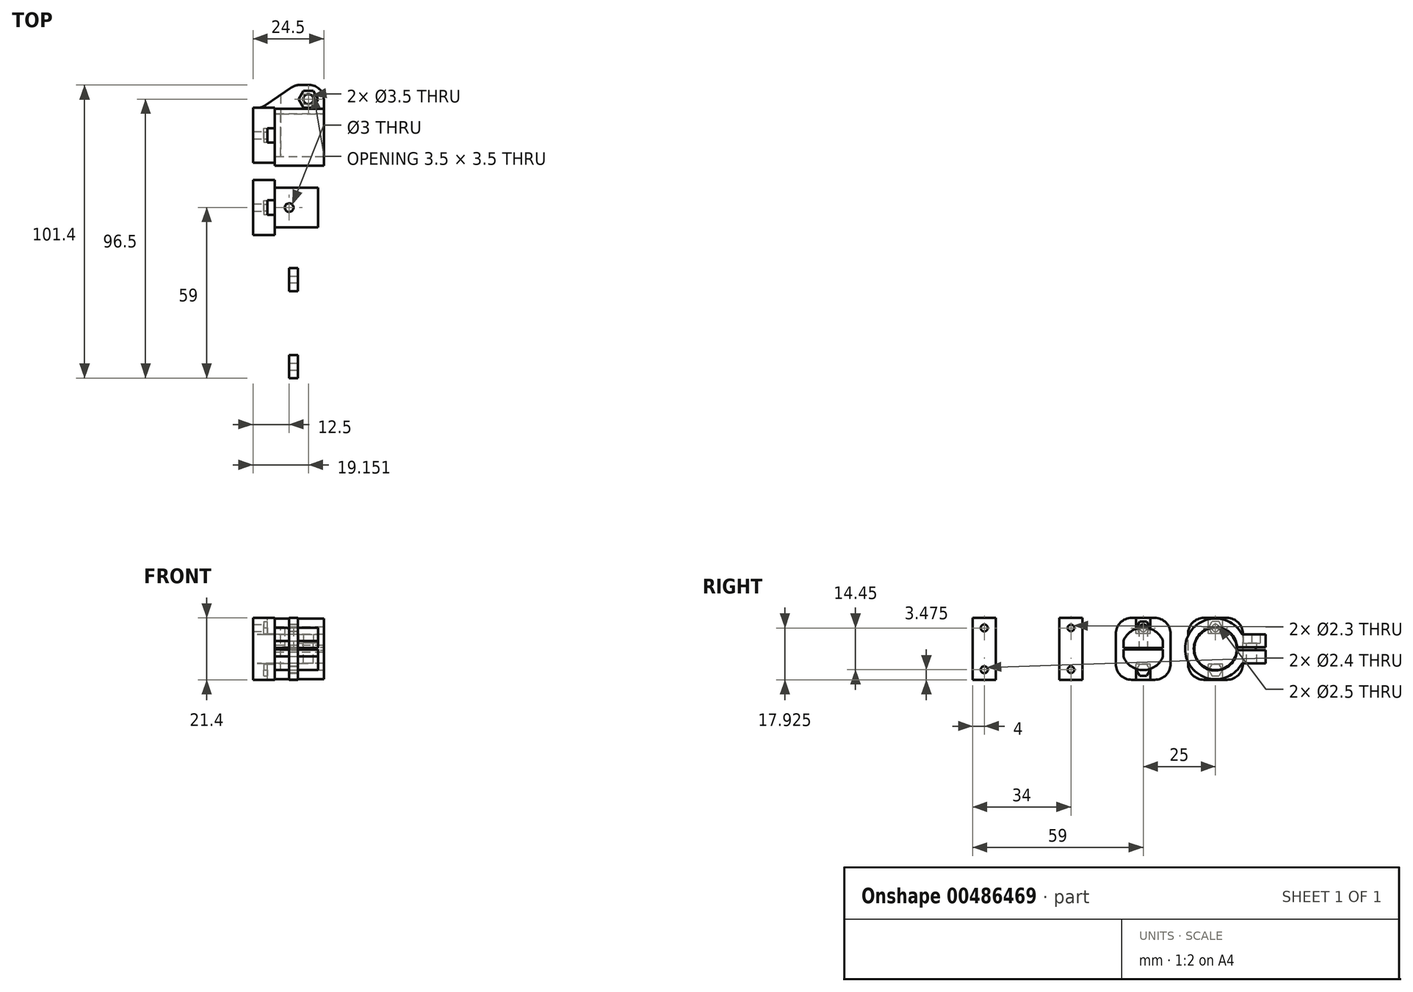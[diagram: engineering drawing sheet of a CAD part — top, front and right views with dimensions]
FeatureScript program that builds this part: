
annotation { "Feature Type Name" : "Feature", "Feature Type Description" : "" }
export const myFeature = defineFeature(function(context is Context, id is Id, definition is map)
    precondition{}
    {
        {
            assignVariable(context, id + "F0", {"name" : "nut_distance", "anyValue" : 5 * mm});
        }
        {
            var Q0;
            Q0=qCreatedBy(makeId("Front.planeOp"),FACE);
            var sketch = newSketch(context, id + "F1", { "sketchPlane" : qUnion([Q0])});
            skLineSegment(sketch, "E0", {"start": v(0, 3.75) * mm, "end": v(-7.5, 3.75) * mm});
            skLineSegment(sketch, "E1", {"start": v(-7.5, -3.75) * mm, "end": v(-7.5, 3.75) * mm});
            skLineSegment(sketch, "E2", {"start": v(-7.5, -3.75) * mm, "end": v(0, -3.75) * mm});
            skLineSegment(sketch, "E3", {"start": v(0, -10.7) * mm, "end": v(0, -3.75) * mm});
            skLineSegment(sketch, "E4", {"start": v(0, -10.7) * mm, "end": v(-12.5, -10.7) * mm});
            skLineSegment(sketch, "E5", {"start": v(-12.5, -10.7) * mm, "end": v(-12.5, 10.7) * mm});
            skLineSegment(sketch, "E6", {"start": v(0, 3.75) * mm, "end": v(0, 10.7) * mm});
            skLineSegment(sketch, "E7", {"start": v(-12.5, 10.7) * mm, "end": v(0, 10.7) * mm});
            skSolve(sketch);
        }
        {
            var Q0;
            Q0=qSketchRegion(id+"F1",true);
            extrude(context, id + "F2", {"entities" : qUnion([Q0]), "depth" : 8 * mm, "offsetDistance" : 25 * mm, "symmetric" : true});
        }
        {
            var Q0;
            Q0=makeQuery(id+"F2.opExtrude","SWEPT_FACE",FACE,{"disambiguationData":[OSD([sQuery(id+"F1.wireOp",EDGE,"E6")])]});
            var sketch = newSketch(context, id + "F3", { "sketchPlane" : qUnion([Q0])});
            skLineSegment(sketch, "E8", {"start": v(-12.42, 0) * mm, "end": v(17.97, 0) * mm, "construction": true});
            skLineSegment(sketch, "E9", {"start": v(0, 22.03) * mm, "end": v(0, -15.29) * mm, "construction": true});
            skPoint(sketch, "E9.startSnap0", {"position": v(0, 10.7) * mm});
            skLineSegment(sketch, "E10", {"start": v(0, 5.25) * mm, "end": v(-1.2, 5.25) * mm});
            skLineSegment(sketch, "E11", {"start": v(-1.2, 5.25) * mm, "end": v(-2.4, 7.32) * mm});
            skLineSegment(sketch, "E12", {"start": v(-2.4, 7.32) * mm, "end": v(0, 7.32) * mm, "construction": true});
            skLineSegment(sketch, "E13", {"start": v(0, 7.32) * mm, "end": v(1.2, 5.25) * mm, "construction": true});
            skLineSegment(sketch, "E14.MirrorCS", {"start": v(-1.2, 9.4) * mm, "end": v(-2.4, 7.32) * mm});
            skLineSegment(sketch, "E15.MirrorCS", {"start": v(0, 9.4) * mm, "end": v(-1.2, 9.4) * mm});
            skLineSegment(sketch, "E16.MirrorCS", {"start": v(0, 9.4) * mm, "end": v(1.2, 9.4) * mm});
            skLineSegment(sketch, "E17.MirrorCS", {"start": v(1.2, 9.4) * mm, "end": v(2.4, 7.33) * mm});
            skLineSegment(sketch, "E18.MirrorCS", {"start": v(1.2, 5.25) * mm, "end": v(2.4, 7.33) * mm});
            skLineSegment(sketch, "E19.MirrorCS", {"start": v(0, 5.25) * mm, "end": v(1.2, 5.25) * mm});
            skLineSegment(sketch, "E20.MirrorCS", {"start": v(-1.2, -9.4) * mm, "end": v(-2.4, -7.32) * mm});
            skLineSegment(sketch, "E21.MirrorCS", {"start": v(0, -9.4) * mm, "end": v(-1.2, -9.4) * mm});
            skLineSegment(sketch, "E22.MirrorCS", {"start": v(0, -9.4) * mm, "end": v(1.2, -9.4) * mm});
            skLineSegment(sketch, "E23.MirrorCS", {"start": v(1.2, -9.4) * mm, "end": v(2.4, -7.33) * mm});
            skLineSegment(sketch, "E24.MirrorCS", {"start": v(1.2, -5.25) * mm, "end": v(2.4, -7.33) * mm});
            skLineSegment(sketch, "E25.MirrorCS", {"start": v(0, -5.25) * mm, "end": v(1.2, -5.25) * mm});
            skLineSegment(sketch, "E26.MirrorCS", {"start": v(0, -5.25) * mm, "end": v(-1.2, -5.25) * mm});
            skLineSegment(sketch, "E27.MirrorCS", {"start": v(-1.2, -5.25) * mm, "end": v(-2.4, -7.32) * mm});
            skSolve(sketch);
        }
        {
            var Q0;
            Q0=makeQuery(id+"F3.imprint","IMPRINT",FACE,{"disambiguationData":[TD([[makeQuery(id+"F3.imprint","IMPRINT",EDGE,{"derivedFrom":sQuery(id+"F3.wireOp",EDGE,"E10")}),-1.0]])]});
            var Q1;
            Q1=makeQuery(id+"F3.imprint","IMPRINT",FACE,{"disambiguationData":[TD([[makeQuery(id+"F3.imprint","IMPRINT",EDGE,{"derivedFrom":sQuery(id+"F3.wireOp",EDGE,"E20.MirrorCS")}),-1.0]])]});
            extrude(context, id + "F4", {"entities" : qUnion([Q0, Q1]), "operationType" : NewBodyOperationType.REMOVE, "oppositeDirection" : true, "depth" : 5.4 * mm, "hasOffset" : true, "offsetDistance" : 4 * mm, "hasSecondDirection" : true, "secondDirectionOppositeDirection" : true, "secondDirectionDepth" : getVariable(context, 'nut_distance') - 1.3 * mm});
        }
        {
            var Q0;
            Q0=makeQuery(id+"F2.opExtrude","SWEPT_FACE",FACE,{"disambiguationData":[OSD([sQuery(id+"F1.wireOp",EDGE,"E7")])]});
            var sketch = newSketch(context, id + "F5", { "sketchPlane" : qUnion([Q0])});
            skLineSegment(sketch, "E28.bottom", {"start": v(-7.5, 2.5) * mm, "end": v(-5, 2.5) * mm});
            skLineSegment(sketch, "E28.top", {"start": v(-7.5, -2.5) * mm, "end": v(-5, -2.5) * mm});
            skLineSegment(sketch, "E28.left", {"start": v(-7.5, 2.5) * mm, "end": v(-7.5, -2.5) * mm});
            skLineSegment(sketch, "E28.right", {"start": v(-5, 2.5) * mm, "end": v(-5, -2.5) * mm});
            skSolve(sketch);
        }
        {
            var Q0;
            Q0=qSketchRegion(id+"F5",true);
            var Q1;
            Q1=makeQuery(id+"F4.boolean.opBoolean","COPY",VERTEX,{"derivedFrom":makeQuery(id+"F4.opExtrude","CAP_VERTEX",VERTEX,{"disambiguationData":[OSD([sQuery(id+"F3.wireOp",EDGE,"E10"),sQuery(id+"F3.wireOp",EDGE,"E11")])],"isStart":false})});
            extrude(context, id + "F6", {"entities" : qUnion([Q0]), "operationType" : NewBodyOperationType.REMOVE, "endBound" : BoundingType.UP_TO_VERTEX, "oppositeDirection" : true, "depth" : 25 * mm, "endBoundEntityVertex" : qUnion([Q1]), "offsetDistance" : 25 * mm});
        }
        {
            var Q0;
            Q0=makeQuery(id+"F2.opExtrude","SWEPT_FACE",FACE,{"disambiguationData":[OSD([sQuery(id+"F1.wireOp",EDGE,"E6")])]});
            var sketch = newSketch(context, id + "F7", { "sketchPlane" : qUnion([Q0])});
            skCircle(sketch, "E29", {"center": v(0, 7.22) * mm, "radius": 1.25 * mm});
            skCircle(sketch, "E30.MirrorC", {"center": v(0, -7.22) * mm, "radius": 1.25 * mm});
            skSolve(sketch);
        }
        {
            var Q0;
            Q0=makeQuery(id+"F7.imprint","IMPRINT",FACE,{"disambiguationData":[TD([[makeQuery(id+"F7.imprint","IMPRINT",EDGE,{"derivedFrom":sQuery(id+"F7.wireOp",EDGE,"E29")}),1.0]])]});
            var Q1;
            Q1=makeQuery(id+"F7.imprint","IMPRINT",FACE,{"disambiguationData":[TD([[makeQuery(id+"F7.imprint","IMPRINT",EDGE,{"derivedFrom":sQuery(id+"F7.wireOp",EDGE,"E30.MirrorC")}),-1.0]])]});
            var Q2;
            Q2=makeQuery(id+"F4.boolean.opBoolean","COPY",VERTEX,{"derivedFrom":makeQuery(id+"F4.opExtrude","CAP_VERTEX",VERTEX,{"disambiguationData":[OSD([sQuery(id+"F3.wireOp",EDGE,"E17.MirrorCS"),sQuery(id+"F3.wireOp",EDGE,"E18.MirrorCS")])],"isStart":false})});
            extrude(context, id + "F8", {"entities" : qUnion([Q0, Q1]), "operationType" : NewBodyOperationType.REMOVE, "endBound" : BoundingType.THROUGH_ALL, "oppositeDirection" : true, "depth" : 25 * mm, "endBoundEntityVertex" : qUnion([Q2]), "offsetDistance" : 25 * mm});
        }
        {
            var Q0;
            Q0=qSketchRegion(id+"F5",true);
            var Q1;
            Q1=makeQuery(id+"F2.opExtrude","SWEPT_FACE",FACE,{"disambiguationData":[OSD([sQuery(id+"F1.wireOp",EDGE,"E4")])]});
            var Q2;
            Q2=makeQuery(id+"F4.boolean.opBoolean","COPY",VERTEX,{"derivedFrom":makeQuery(id+"F4.opExtrude","CAP_VERTEX",VERTEX,{"disambiguationData":[OSD([sQuery(id+"F3.wireOp",EDGE,"E26.MirrorCS"),sQuery(id+"F3.wireOp",EDGE,"E27.MirrorCS")])],"isStart":false})});
            extrude(context, id + "F9", {"entities" : qUnion([Q0]), "operationType" : NewBodyOperationType.REMOVE, "endBound" : BoundingType.UP_TO_SURFACE, "oppositeDirection" : true, "depth" : 25 * mm, "endBoundEntityFace" : qUnion([Q1]), "offsetDistance" : 25 * mm, "hasSecondDirection" : true, "secondDirectionBound" : BoundingType.UP_TO_VERTEX, "secondDirectionOppositeDirection" : true, "secondDirectionDepth" : 25 * mm, "secondDirectionBoundEntityVertex" : qUnion([Q2])});
        }
        {
            var Q0;
            Q0=qSketchRegion(id+"F3",true);
            extrude(context, id + "F10", {"entities" : qUnion([Q0]), "operationType" : NewBodyOperationType.REMOVE, "oppositeDirection" : true, "depth" : (7.5 + 1.3) * mm, "offsetDistance" : 25 * mm, "hasSecondDirection" : true, "secondDirectionOppositeDirection" : true, "secondDirectionDepth" : (5.4 + 1.7) * mm});
        }
        {
            var Q0;
            Q0=qCreatedBy(makeId("Front.planeOp"),FACE);
            cPlane(context, id + "F11", {"entities" : qUnion([Q0]), "cplaneType" : CPlaneType.OFFSET, "offset" : 25 * mm, "width" : 150 * mm, "height" : 150 * mm});
        }
        {
            var Q0;
            Q0=qCreatedBy(makeId("Right.planeOp"),FACE);
            var sketch = newSketch(context, id + "F12", { "sketchPlane" : qUnion([Q0])});
            skLineSegment(sketch, "E31.bottom", {"start": v(-21, 10.7) * mm, "end": v(-29, 10.7) * mm});
            skLineSegment(sketch, "E31.top", {"start": v(-21, -10.7) * mm, "end": v(-29, -10.7) * mm});
            skLineSegment(sketch, "E31.left", {"start": v(-21, 10.7) * mm, "end": v(-21, -10.7) * mm});
            skLineSegment(sketch, "E31.right", {"start": v(-29, 10.7) * mm, "end": v(-29, -10.7) * mm});
            skCircle(sketch, "E32", {"center": v(-25, 7.22) * mm, "radius": 1.15 * mm});
            skCircle(sketch, "E33.MirrorC", {"center": v(-25, -7.22) * mm, "radius": 1.15 * mm});
            skSolve(sketch);
        }
        {
            var Q0;
            Q0=makeQuery(id+"F12.imprint","IMPRINT",FACE,{"disambiguationData":[TD([[makeQuery(id+"F12.imprint","IMPRINT",EDGE,{"derivedFrom":sQuery(id+"F12.wireOp",EDGE,"E31.bottom")}),1.0]])]});
            extrude(context, id + "F13", {"entities" : qUnion([Q0]), "depth" : 3 * mm, "offsetDistance" : 25 * mm});
        }
        {
            var Q0;
            Q0=qCreatedBy(id+"F11.planeOp",FACE);
            var sketch = newSketch(context, id + "F14", { "sketchPlane" : qUnion([Q0])});
            skArc(sketch, "E34", {"start": v(0, 3.75) * mm, "mid": v(-0.1, 0) * mm, "end": v(0, -3.75) * mm});
            skLineSegment(sketch, "E35", {"start": v(0, 3.75) * mm, "end": v(0, -3.75) * mm});
            skSolve(sketch);
        }
        {
            var Q0;
            Q0=makeQuery(id+"F13.opExtrude","SWEPT_BODY",BODY,{"disambiguationData":[OSD([sQuery(id+"F12.wireOp",EDGE,"E31.bottom"),sQuery(id+"F12.wireOp",EDGE,"E31.top"),sQuery(id+"F12.wireOp",EDGE,"E31.left"),sQuery(id+"F12.wireOp",EDGE,"E31.right"),sQuery(id+"F12.wireOp",EDGE,"E32"),sQuery(id+"F12.wireOp",EDGE,"E33.MirrorC")])]});
            transform(context, id + "F15", {"entities" : qUnion([Q0]), "transformType" : TransformType.TRANSLATION_3D, "dx" : 0 * mm, "dy" : -30 * mm, "dz" : 0 * mm, "makeCopy" : true});
        }
        {
            var Q0;
            Q0=makeQuery(id+"F15.opPattern","COPY",FACE,{"derivedFrom":makeQuery(id+"F13.opExtrude","CAP_FACE",FACE,{"disambiguationData":[OSD([sQuery(id+"F12.wireOp",EDGE,"E31.bottom"),sQuery(id+"F12.wireOp",EDGE,"E31.top"),sQuery(id+"F12.wireOp",EDGE,"E31.left"),sQuery(id+"F12.wireOp",EDGE,"E31.right"),sQuery(id+"F12.wireOp",EDGE,"E32"),sQuery(id+"F12.wireOp",EDGE,"E33.MirrorC")])],"isStart":false}),"instanceName":"1"});
            var sketch = newSketch(context, id + "F16", { "sketchPlane" : qUnion([Q0])});
            skCircle(sketch, "E36", {"center": v(-55, 7.22) * mm, "radius": 1.2 * mm});
            skCircle(sketch, "E37.MirrorC", {"center": v(-55, -7.22) * mm, "radius": 1.2 * mm});
            skSolve(sketch);
        }
        {
            var Q0;
            Q0=qSketchRegion(id+"F16",true);
            extrude(context, id + "F17", {"entities" : qUnion([Q0]), "operationType" : NewBodyOperationType.REMOVE, "endBound" : BoundingType.THROUGH_ALL, "oppositeDirection" : true, "depth" : 25 * mm, "offsetDistance" : 25 * mm});
        }
        {
            var Q0;
            Q0=qCreatedBy(makeId("Right.planeOp"),FACE);
            var sketch = newSketch(context, id + "F18", { "sketchPlane" : qUnion([Q0])});
            skCircle(sketch, "E38", {"center": v(0, 0) * mm, "radius": 7.35 * mm});
            skSolve(sketch);
        }
        {
            var Q0;
            Q0=makeQuery(id+"F2.opExtrude","SWEPT_FACE",FACE,{"disambiguationData":[OSD([sQuery(id+"F1.wireOp",EDGE,"E1")])]});
            var sketch = newSketch(context, id + "F19", { "sketchPlane" : qUnion([Q0])});
            skLineSegment(sketch, "E39.bottom", {"start": v(4, 3.75) * mm, "end": v(-4, 3.75) * mm});
            skLineSegment(sketch, "E39.top", {"start": v(4, -3.75) * mm, "end": v(-4, -3.75) * mm});
            skLineSegment(sketch, "E39.left", {"start": v(4, 3.75) * mm, "end": v(4, -3.75) * mm});
            skLineSegment(sketch, "E39.right", {"start": v(-4, 3.75) * mm, "end": v(-4, -3.75) * mm});
            skSolve(sketch);
        }
        {
            var Q0;
            Q0=qSketchRegion(id+"F19",true);
            var Q1;
            Q1=makeQuery(id+"F2.opExtrude","SWEPT_FACE",FACE,{"disambiguationData":[OSD([sQuery(id+"F1.wireOp",EDGE,"E6")])]});
            extrude(context, id + "F20", {"entities" : qUnion([Q0]), "operationType" : NewBodyOperationType.ADD, "endBound" : BoundingType.UP_TO_SURFACE, "depth" : 25 * mm, "endBoundEntityFace" : qUnion([Q1]), "offsetDistance" : 25 * mm});
        }
        {
            var Q0;
            Q0=qSketchRegion(id+"F18",true);
            extrude(context, id + "F21", {"entities" : qUnion([Q0]), "operationType" : NewBodyOperationType.ADD, "oppositeDirection" : true, "depth" : 5 * mm, "offsetDistance" : 25 * mm, "hasSecondDirection" : true, "secondDirectionOppositeDirection" : false, "secondDirectionDepth" : 10 * mm});
        }
        {
            var Q0;
            {var subQ0=sQuery(id+"F1.wireOp",EDGE,"E7");var subQ1=sQuery(id+"F1.wireOp",EDGE,"E6");var subQ4=sQuery(id+"F1.wireOp",EDGE,"E3");var subQ8=makeQuery(id+"F2.opExtrude","SWEPT_FACE",FACE,{"disambiguationData":[OSD([subQ1])]});var subQ9=sQuery(id+"F19.wireOp",EDGE,"E39.left");var subQ10=sQuery(id+"F19.wireOp",EDGE,"E39.right");Q0=makeQuery(id+"F21.boolean.opBoolean","SPLIT",FACE,{"disambiguationData":[TD([makeQuery(id+"F2.opExtrude","SWEPT_FACE",FACE,{"disambiguationData":[OSD([subQ0])]})])],"derivedFrom":makeQuery(id+"F20.boolean.opBoolean","MERGE",FACE,{"derivedFrom":[makeQuery(id+"F2.opExtrude","SWEPT_FACE",FACE,{"disambiguationData":[OSD([subQ4])]}),subQ8,makeQuery(id+"F20.opExtrude","CAP_FACE",FACE,{"disambiguationData":[OSD([sQuery(id+"F19.wireOp",EDGE,"E39.bottom"),sQuery(id+"F19.wireOp",EDGE,"E39.top"),subQ9,subQ10])],"isStart":false})]})});}
            var sketch = newSketch(context, id + "F22", { "sketchPlane" : qUnion([Q0])});
            skArc(sketch, "E40", {"start": v(4, 6.17) * mm, "mid": v(0, 7.35) * mm, "end": v(-4, 6.17) * mm});
            skLineSegment(sketch, "E41", {"start": v(-4, 6.17) * mm, "end": v(-4, 10.7) * mm});
            skLineSegment(sketch, "E42", {"start": v(-4, 10.7) * mm, "end": v(4, 10.7) * mm});
            skLineSegment(sketch, "E43", {"start": v(4, 10.7) * mm, "end": v(4, 6.17) * mm});
            skArc(sketch, "E44.MirrorCS", {"start": v(4, -6.17) * mm, "mid": v(0, -7.35) * mm, "end": v(-4, -6.17) * mm});
            skLineSegment(sketch, "E45.MirrorCS", {"start": v(-4, -10.7) * mm, "end": v(4, -10.7) * mm});
            skLineSegment(sketch, "E46.MirrorCS", {"start": v(-4, -6.17) * mm, "end": v(-4, -10.7) * mm});
            skLineSegment(sketch, "E47.MirrorCS", {"start": v(4, -10.7) * mm, "end": v(4, -6.17) * mm});
            skSolve(sketch);
        }
        {
            var Q0;
            Q0=qSketchRegion(id+"F22",true);
            extrude(context, id + "F23", {"entities" : qUnion([Q0]), "operationType" : NewBodyOperationType.REMOVE, "oppositeDirection" : true, "depth" : 5 * mm, "offsetDistance" : 25 * mm});
        }
        {
            var Q0;
            Q0=makeQuery(id+"F2.opExtrude","SWEPT_FACE",FACE,{"disambiguationData":[OSD([sQuery(id+"F1.wireOp",EDGE,"E5")])]});
            var sketch = newSketch(context, id + "F24", { "sketchPlane" : qUnion([Q0])});
            skPoint(sketch, "E48", {"position": v(4, -10.7) * mm});
            skPoint(sketch, "E49", {"position": v(4, 10.7) * mm});
            skLineSegment(sketch, "E50.bottom", {"start": v(9.5, -10.7) * mm, "end": v(4, -10.7) * mm});
            skLineSegment(sketch, "E50.top", {"start": v(9.5, 10.7) * mm, "end": v(4, 10.7) * mm});
            skLineSegment(sketch, "E50.left", {"start": v(9.5, -10.7) * mm, "end": v(9.5, 10.7) * mm});
            skLineSegment(sketch, "E50.right", {"start": v(4, -10.7) * mm, "end": v(4, 10.7) * mm});
            skPoint(sketch, "E51.MirrorP", {"position": v(-4, 10.7) * mm});
            skPoint(sketch, "E52.MirrorP", {"position": v(-4, -10.7) * mm});
            skLineSegment(sketch, "E53.MirrorCS", {"start": v(-9.5, -10.7) * mm, "end": v(-4, -10.7) * mm});
            skLineSegment(sketch, "E54.MirrorCS", {"start": v(-4, -10.7) * mm, "end": v(-4, 10.7) * mm});
            skLineSegment(sketch, "E55.MirrorCS", {"start": v(-9.5, -10.7) * mm, "end": v(-9.5, 10.7) * mm});
            skLineSegment(sketch, "E56.MirrorCS", {"start": v(-9.5, 10.7) * mm, "end": v(-4, 10.7) * mm});
            skSolve(sketch);
        }
        {
            var Q0;
            Q0=qSketchRegion(id+"F24",true);
            var Q1;
            {var subQ0=sQuery(id+"F18.wireOp",EDGE,"E38");Q1=makeQuery(id+"F21.boolean.opBoolean","SPLIT",FACE,{"disambiguationData":[TD([makeQuery(id+"F20.opExtrude","SWEPT_FACE",FACE,{"disambiguationData":[OSD([sQuery(id+"F19.wireOp",EDGE,"E39.right")])]})])],"derivedFrom":makeQuery(id+"F21.opExtrude","CAP_FACE",FACE,{"disambiguationData":[OSD([subQ0])],"isStart":false})});}
            extrude(context, id + "F25", {"entities" : qUnion([Q0]), "operationType" : NewBodyOperationType.ADD, "endBound" : BoundingType.UP_TO_SURFACE, "oppositeDirection" : true, "depth" : 5 * mm, "endBoundEntityFace" : qUnion([Q1]), "offsetDistance" : 25 * mm});
        }
        {
            var Q0;
            Q0=makeQuery(id+"F25.opExtrude","SWEPT_EDGE",EDGE,{"disambiguationData":[OSD([sQuery(id+"F24.wireOp",EDGE,"E50.top"),sQuery(id+"F24.wireOp",EDGE,"E50.left")])]});
            var Q1;
            Q1=makeQuery(id+"F25.opExtrude","SWEPT_EDGE",EDGE,{"disambiguationData":[OSD([sQuery(id+"F24.wireOp",EDGE,"E55.MirrorCS"),sQuery(id+"F24.wireOp",EDGE,"E56.MirrorCS")])]});
            var Q2;
            Q2=makeQuery(id+"F25.opExtrude","SWEPT_EDGE",EDGE,{"disambiguationData":[OSD([sQuery(id+"F24.wireOp",EDGE,"E53.MirrorCS"),sQuery(id+"F24.wireOp",EDGE,"E55.MirrorCS")])]});
            var Q3;
            Q3=makeQuery(id+"F25.opExtrude","SWEPT_EDGE",EDGE,{"disambiguationData":[OSD([sQuery(id+"F24.wireOp",EDGE,"E50.bottom"),sQuery(id+"F24.wireOp",EDGE,"E50.left")])]});
            fillet(context, id + "F26", {"entities" : qUnion([Q0, Q1, Q2, Q3]), "radius" : 5.5 * mm, "tangentPropagation" : true, "allowEdgeOverflow" : false});
        }
        {
            var Q0;
            Q0=qCreatedBy(makeId("Top.planeOp"),FACE);
            var sketch = newSketch(context, id + "F27", { "sketchPlane" : qUnion([Q0])});
            skCircle(sketch, "E57", {"center": v(0, 0) * mm, "radius": 1.5 * mm});
            skSolve(sketch);
        }
        {
            var Q0;
            Q0=qSketchRegion(id+"F27",true);
            extrude(context, id + "F28", {"entities" : qUnion([Q0]), "operationType" : NewBodyOperationType.REMOVE, "depth" : 25 * mm, "offsetDistance" : 25 * mm, "hasSecondDirection" : true, "secondDirectionOppositeDirection" : false, "secondDirectionDepth" : 0 * mm});
        }
        {
            var Q0;
            Q0=qCreatedBy(makeId("Front.planeOp"),FACE);
            cPlane(context, id + "F29", {"entities" : qUnion([Q0]), "cplaneType" : CPlaneType.OFFSET, "offset" : 25 * mm, "oppositeDirection" : true, "width" : 150 * mm, "height" : 150 * mm});
        }
        {
            var Q0;
            Q0=makeQuery(id+"F2.opExtrude","SWEPT_BODY",BODY,{"disambiguationData":[OSD([sQuery(id+"F1.wireOp",EDGE,"E0"),sQuery(id+"F1.wireOp",EDGE,"E1"),sQuery(id+"F1.wireOp",EDGE,"E2"),sQuery(id+"F1.wireOp",EDGE,"E3"),sQuery(id+"F1.wireOp",EDGE,"E4"),sQuery(id+"F1.wireOp",EDGE,"E5"),sQuery(id+"F1.wireOp",EDGE,"E6"),sQuery(id+"F1.wireOp",EDGE,"E7")])]});
            transform(context, id + "F30", {"entities" : qUnion([Q0]), "transformType" : TransformType.TRANSLATION_3D, "dx" : 0 * mm, "dy" : 25 * mm, "dz" : 0 * mm, "makeCopy" : true});
        }
        {
            var Q0;
            Q0=qCreatedBy(makeId("Right.planeOp"),FACE);
            var sketch = newSketch(context, id + "F31", { "sketchPlane" : qUnion([Q0])});
            skCircle(sketch, "E58", {"center": v(25, 0) * mm, "radius": 7.35 * mm});
            skSolve(sketch);
        }
        {
            var Q0;
            Q0=qCreatedBy(makeId("Right.planeOp"),FACE);
            var sketch = newSketch(context, id + "F32", { "sketchPlane" : qUnion([Q0])});
            skCircle(sketch, "E59", {"center": v(25, 0) * mm, "radius": 7.5 * mm});
            skCircle(sketch, "E60", {"center": v(25, 0) * mm, "radius": 10.5 * mm});
            skSolve(sketch);
        }
        {
            var Q0;
            Q0=qSketchRegion(id+"F32",true);
            extrude(context, id + "F33", {"entities" : qUnion([Q0]), "operationType" : NewBodyOperationType.ADD, "depth" : 12 * mm, "offsetDistance" : 25 * mm, "hasSecondDirection" : true, "secondDirectionOppositeDirection" : true, "secondDirectionDepth" : 5 * mm});
        }
        {
            var Q0;
            Q0=qSketchRegion(id+"F31",true);
            extrude(context, id + "F34", {"entities" : qUnion([Q0]), "operationType" : NewBodyOperationType.REMOVE, "oppositeDirection" : true, "depth" : 3 * mm, "offsetDistance" : 25 * mm, "hasSecondDirection" : true, "secondDirectionOppositeDirection" : false, "secondDirectionDepth" : 10 * mm});
        }
        {
            var Q0;
            Q0=makeQuery(id+"F21.opExtrude","CAP_FACE",FACE,{"disambiguationData":[OSD([sQuery(id+"F18.wireOp",EDGE,"E38")])],"isStart":true});
            var sketch = newSketch(context, id + "F35", { "sketchPlane" : qUnion([Q0])});
            skLineSegment(sketch, "E61.bottom", {"start": v(-9.5, 0.25) * mm, "end": v(9.5, 0.25) * mm});
            skLineSegment(sketch, "E61.top", {"start": v(-9.5, -0.25) * mm, "end": v(9.5, -0.25) * mm});
            skLineSegment(sketch, "E61.left", {"start": v(-9.5, 0.25) * mm, "end": v(-9.5, -0.25) * mm});
            skLineSegment(sketch, "E61.right", {"start": v(9.5, 0.25) * mm, "end": v(9.5, -0.25) * mm});
            skLineSegment(sketch, "E62", {"start": v(6.85, 0.25) * mm, "end": v(6.85, 2.66) * mm});
            skLineSegment(sketch, "E63", {"start": v(6.85, 2.66) * mm, "end": v(9.5, 2.66) * mm});
            skLineSegment(sketch, "E64", {"start": v(9.5, 2.66) * mm, "end": v(9.5, 0.25) * mm});
            skLineSegment(sketch, "E65.MirrorCS", {"start": v(6.85, -2.66) * mm, "end": v(9.5, -2.66) * mm});
            skLineSegment(sketch, "E66.MirrorCS", {"start": v(9.5, -2.66) * mm, "end": v(9.5, -0.25) * mm});
            skLineSegment(sketch, "E67.MirrorCS", {"start": v(6.85, -0.25) * mm, "end": v(6.85, -2.66) * mm});
            skLineSegment(sketch, "E68.MirrorCS", {"start": v(-6.85, 0.25) * mm, "end": v(-6.85, 2.66) * mm});
            skLineSegment(sketch, "E69.MirrorCS", {"start": v(-6.85, 2.66) * mm, "end": v(-9.5, 2.66) * mm});
            skLineSegment(sketch, "E70.MirrorCS", {"start": v(-9.5, 2.66) * mm, "end": v(-9.5, 0.25) * mm});
            skLineSegment(sketch, "E71.MirrorCS", {"start": v(-9.5, -2.66) * mm, "end": v(-9.5, -0.25) * mm});
            skLineSegment(sketch, "E72.MirrorCS", {"start": v(-6.85, -2.66) * mm, "end": v(-9.5, -2.66) * mm});
            skLineSegment(sketch, "E73.MirrorCS", {"start": v(-6.85, -0.25) * mm, "end": v(-6.85, -2.66) * mm});
            skSolve(sketch);
        }
        {
            var Q0;
            Q0=qSketchRegion(id+"F35",true);
            var Q1;
            {var subQ0=sQuery(id+"F5.wireOp",EDGE,"E28.top");var subQ8=sQuery(id+"F22.wireOp",EDGE,"E44.MirrorCS");var subQ11=sQuery(id+"F22.wireOp",EDGE,"E40");Q1=makeQuery(id+"F25.boolean.opBoolean","MERGE",FACE,{"derivedFrom":[makeQuery(id+"F23.boolean.opBoolean","COPY",FACE,{"disambiguationData":[TD([makeQuery(id+"F6.boolean.opBoolean","COPY",FACE,{"derivedFrom":makeQuery(id+"F6.opExtrude","SWEPT_FACE",FACE,{"disambiguationData":[OSD([subQ0])]})})])],"derivedFrom":makeQuery(id+"F23.opExtrude","CAP_FACE",FACE,{"disambiguationData":[OSD([subQ11,sQuery(id+"F22.wireOp",EDGE,"E41"),sQuery(id+"F22.wireOp",EDGE,"E42"),sQuery(id+"F22.wireOp",EDGE,"E43")])],"isStart":false})}),makeQuery(id+"F23.boolean.opBoolean","COPY",FACE,{"disambiguationData":[TD([makeQuery(id+"F9.boolean.opBoolean","COPY",FACE,{"derivedFrom":makeQuery(id+"F9.opExtrude","SWEPT_FACE",FACE,{"disambiguationData":[OSD([subQ0])]})})])],"derivedFrom":makeQuery(id+"F23.opExtrude","CAP_FACE",FACE,{"disambiguationData":[OSD([subQ8,sQuery(id+"F22.wireOp",EDGE,"E45.MirrorCS"),sQuery(id+"F22.wireOp",EDGE,"E46.MirrorCS"),sQuery(id+"F22.wireOp",EDGE,"E47.MirrorCS")])],"isStart":false})}),makeQuery(id+"F25.opExtrude","CAP_FACE",FACE,{"disambiguationData":[OSD([sQuery(id+"F24.wireOp",EDGE,"E50.bottom"),sQuery(id+"F24.wireOp",EDGE,"E50.top"),sQuery(id+"F24.wireOp",EDGE,"E50.left"),sQuery(id+"F24.wireOp",EDGE,"E50.right")])],"isStart":false})]});}
            extrude(context, id + "F36", {"entities" : qUnion([Q0]), "operationType" : NewBodyOperationType.REMOVE, "endBound" : BoundingType.UP_TO_SURFACE, "oppositeDirection" : true, "depth" : 25 * mm, "endBoundEntityFace" : qUnion([Q1]), "offsetDistance" : 25 * mm});
        }
        {
            var Q0;
            Q0=qCreatedBy(id+"F29.planeOp",FACE);
            cPlane(context, id + "F37", {"entities" : qUnion([Q0]), "cplaneType" : CPlaneType.OFFSET, "offset" : (14.8 / 2) * mm, "oppositeDirection" : true, "width" : 150 * mm, "height" : 150 * mm});
        }
        {
            var Q0;
            Q0=qCreatedBy(makeId("Top.planeOp"),FACE);
            var sketch = newSketch(context, id + "F38", { "sketchPlane" : qUnion([Q0])});
            skLineSegment(sketch, "E74", {"start": v(-12.5, 32.4) * mm, "end": v(2, 42.4) * mm});
            skLineSegment(sketch, "E75", {"start": v(2, 42.4) * mm, "end": v(12, 42.4) * mm});
            skLineSegment(sketch, "E76", {"start": v(12, 42.4) * mm, "end": v(12, 32.4) * mm});
            skLineSegment(sketch, "E77", {"start": v(12, 32.4) * mm, "end": v(-12.5, 32.4) * mm});
            skSolve(sketch);
        }
        {
            var Q0;
            Q0=makeQuery(id+"F38.imprint","IMPRINT",FACE,{"disambiguationData":[TD([[makeQuery(id+"F38.imprint","IMPRINT",EDGE,{"derivedFrom":sQuery(id+"F38.wireOp",EDGE,"E74")}),-1.0]])]});
            var sketch = newSketch(context, id + "F39", { "sketchPlane" : qUnion([Q0])});
            skCircle(sketch, "E78.cCircle", {"center": v(6.65, 37.5) * mm, "radius": 2.9 * mm, "construction": true});
            skLineSegment(sketch, "E78.0", {"start": v(4.98, 40.4) * mm, "end": v(8.33, 40.4) * mm});
            skLineSegment(sketch, "E78.1", {"start": v(8.33, 40.4) * mm, "end": v(10, 37.5) * mm});
            skLineSegment(sketch, "E78.2", {"start": v(10, 37.5) * mm, "end": v(8.33, 34.6) * mm});
            skLineSegment(sketch, "E78.3", {"start": v(8.33, 34.6) * mm, "end": v(4.98, 34.6) * mm});
            skLineSegment(sketch, "E78.4", {"start": v(4.98, 34.6) * mm, "end": v(3.3, 37.5) * mm});
            skLineSegment(sketch, "E78.5", {"start": v(3.3, 37.5) * mm, "end": v(4.98, 40.4) * mm});
            skPoint(sketch, "E78.0.midPoint", {"position": v(6.65, 40.4) * mm});
            skSolve(sketch);
        }
        {
            var Q0;
            Q0=makeQuery(id+"F38.imprint","IMPRINT",FACE,{"disambiguationData":[TD([[makeQuery(id+"F38.imprint","IMPRINT",EDGE,{"derivedFrom":sQuery(id+"F38.wireOp",EDGE,"E74")}),-1.0]])]});
            var sketch = newSketch(context, id + "F40", { "sketchPlane" : qUnion([Q0])});
            skCircle(sketch, "E79", {"center": v(6.65, 37.5) * mm, "radius": 1.75 * mm});
            skSolve(sketch);
        }
        {
            var Q0;
            Q0 = qSketchRegion(id + "F38", true);
            extrude(context, id + "F41", {"entities" : qUnion([Q0]), "operationType" : NewBodyOperationType.ADD, "depth" : 10 * mm, "offsetDistance" : 25 * mm, "symmetric" : true});
        }
        {
            var Q0;
            Q0 = qSketchRegion(id + "F39", true);
            var Q1;
            Q1=makeQuery(id+"F41.opExtrude","CAP_FACE",FACE,{"disambiguationData":[OSD([sQuery(id+"F38.wireOp",EDGE,"E74"),sQuery(id+"F38.wireOp",EDGE,"E75"),sQuery(id+"F38.wireOp",EDGE,"E76"),sQuery(id+"F38.wireOp",EDGE,"E77")])],"isStart":false});
            extrude(context, id + "F42", {"entities" : qUnion([Q0]), "operationType" : NewBodyOperationType.REMOVE, "endBound" : BoundingType.UP_TO_SURFACE, "depth" : 25 * mm, "endBoundEntityFace" : qUnion([Q1]), "offsetDistance" : 25 * mm, "hasSecondDirection" : true, "secondDirectionOppositeDirection" : false, "secondDirectionDepth" : 2 * mm});
        }
        {
            var Q0;
            Q0 = qSketchRegion(id + "F40", true);
            extrude(context, id + "F43", {"entities" : qUnion([Q0]), "operationType" : NewBodyOperationType.REMOVE, "endBound" : BoundingType.THROUGH_ALL, "oppositeDirection" : true, "depth" : 25 * mm, "offsetDistance" : 25 * mm, "hasSecondDirection" : true, "secondDirectionOppositeDirection" : false, "secondDirectionDepth" : 25 * mm});
        }
        {
            var Q0;
            Q0=makeQuery(id+"F41.boolean.opBoolean","MERGE",FACE,{"derivedFrom":[makeQuery(id+"F33.opExtrude","CAP_FACE",FACE,{"disambiguationData":[OSD([sQuery(id+"F32.wireOp",EDGE,"E59"),sQuery(id+"F32.wireOp",EDGE,"E60")])],"isStart":false}),makeQuery(id+"F41.opExtrude","SWEPT_FACE",FACE,{"disambiguationData":[OSD([sQuery(id+"F38.wireOp",EDGE,"E76")])]})]});
            var sketch = newSketch(context, id + "F44", { "sketchPlane" : qUnion([Q0])});
            skLineSegment(sketch, "E80.bottom", {"start": v(25, 0.5) * mm, "end": v(42.4, 0.5) * mm});
            skLineSegment(sketch, "E80.top", {"start": v(25, -0.5) * mm, "end": v(42.4, -0.5) * mm});
            skLineSegment(sketch, "E80.left", {"start": v(25, 0.5) * mm, "end": v(25, -0.5) * mm});
            skLineSegment(sketch, "E80.right", {"start": v(42.4, 0.5) * mm, "end": v(42.4, -0.5) * mm});
            skSolve(sketch);
        }
        {
            var Q0;
            Q0 = qSketchRegion(id + "F44", true);
            var Q1;
            Q1=makeQuery(id+"F34.boolean.opBoolean","COPY",FACE,{"derivedFrom":makeQuery(id+"F34.opExtrude","CAP_FACE",FACE,{"disambiguationData":[OSD([sQuery(id+"F31.wireOp",EDGE,"E58")])],"isStart":false})});
            extrude(context, id + "F45", {"entities" : qUnion([Q0]), "operationType" : NewBodyOperationType.REMOVE, "endBound" : BoundingType.UP_TO_SURFACE, "oppositeDirection" : true, "depth" : 25 * mm, "endBoundEntityFace" : qUnion([Q1]), "offsetDistance" : 25 * mm});
        }
        {
            var Q0;
            {var subQ0=sQuery(id+"F38.wireOp",EDGE,"E76");var subQ1=sQuery(id+"F38.wireOp",EDGE,"E75");Q0=makeQuery(id+"F45.boolean.opBoolean","SPLIT",EDGE,{"disambiguationData":[TD([makeQuery(id+"F45.opExtrude","SWEPT_FACE",FACE,{"disambiguationData":[OSD([sQuery(id+"F44.wireOp",EDGE,"E80.bottom")])]})])],"derivedFrom":makeQuery(id+"F41.opExtrude","SWEPT_EDGE",EDGE,{"disambiguationData":[OSD([subQ1,subQ0])]})});}
            var Q1;
            {var subQ0=sQuery(id+"F38.wireOp",EDGE,"E76");var subQ1=sQuery(id+"F38.wireOp",EDGE,"E75");Q1=makeQuery(id+"F45.boolean.opBoolean","SPLIT",EDGE,{"disambiguationData":[TD([makeQuery(id+"F45.opExtrude","SWEPT_FACE",FACE,{"disambiguationData":[OSD([sQuery(id+"F44.wireOp",EDGE,"E80.top")])]})])],"derivedFrom":makeQuery(id+"F41.opExtrude","SWEPT_EDGE",EDGE,{"disambiguationData":[OSD([subQ1,subQ0])]})});}
            var Q2;
            {var subQ0=sQuery(id+"F38.wireOp",EDGE,"E74");var subQ1=sQuery(id+"F38.wireOp",EDGE,"E75");Q2=makeQuery(id+"F45.boolean.opBoolean","SPLIT",EDGE,{"disambiguationData":[TD([makeQuery(id+"F45.opExtrude","SWEPT_FACE",FACE,{"disambiguationData":[OSD([sQuery(id+"F44.wireOp",EDGE,"E80.top")])]})])],"derivedFrom":makeQuery(id+"F41.opExtrude","SWEPT_EDGE",EDGE,{"disambiguationData":[OSD([subQ0,subQ1])]})});}
            var Q3;
            {var subQ0=sQuery(id+"F38.wireOp",EDGE,"E74");var subQ1=sQuery(id+"F38.wireOp",EDGE,"E75");Q3=makeQuery(id+"F45.boolean.opBoolean","SPLIT",EDGE,{"disambiguationData":[TD([makeQuery(id+"F45.opExtrude","SWEPT_FACE",FACE,{"disambiguationData":[OSD([sQuery(id+"F44.wireOp",EDGE,"E80.bottom")])]})])],"derivedFrom":makeQuery(id+"F41.opExtrude","SWEPT_EDGE",EDGE,{"disambiguationData":[OSD([subQ0,subQ1])]})});}
            var Q4;
            Q4=makeQuery(id+"F41.boolean.opBoolean","INTERSECT",EDGE,{"derivedFrom":[makeQuery(id+"F30.opPattern","COPY",FACE,{"derivedFrom":makeQuery(id+"F25.opExtrude","SWEPT_FACE",FACE,{"disambiguationData":[OSD([sQuery(id+"F24.wireOp",EDGE,"E55.MirrorCS")])]}),"instanceName":"1"}),makeQuery(id+"F41.opExtrude","SWEPT_FACE",FACE,{"disambiguationData":[OSD([sQuery(id+"F38.wireOp",EDGE,"E74")])]})]});
            fillet(context, id + "F46", {"entities" : qUnion([Q0, Q1, Q2, Q3, Q4]), "radius" : 5 * mm, "tangentPropagation" : true, "allowEdgeOverflow" : false});
        }
    });
